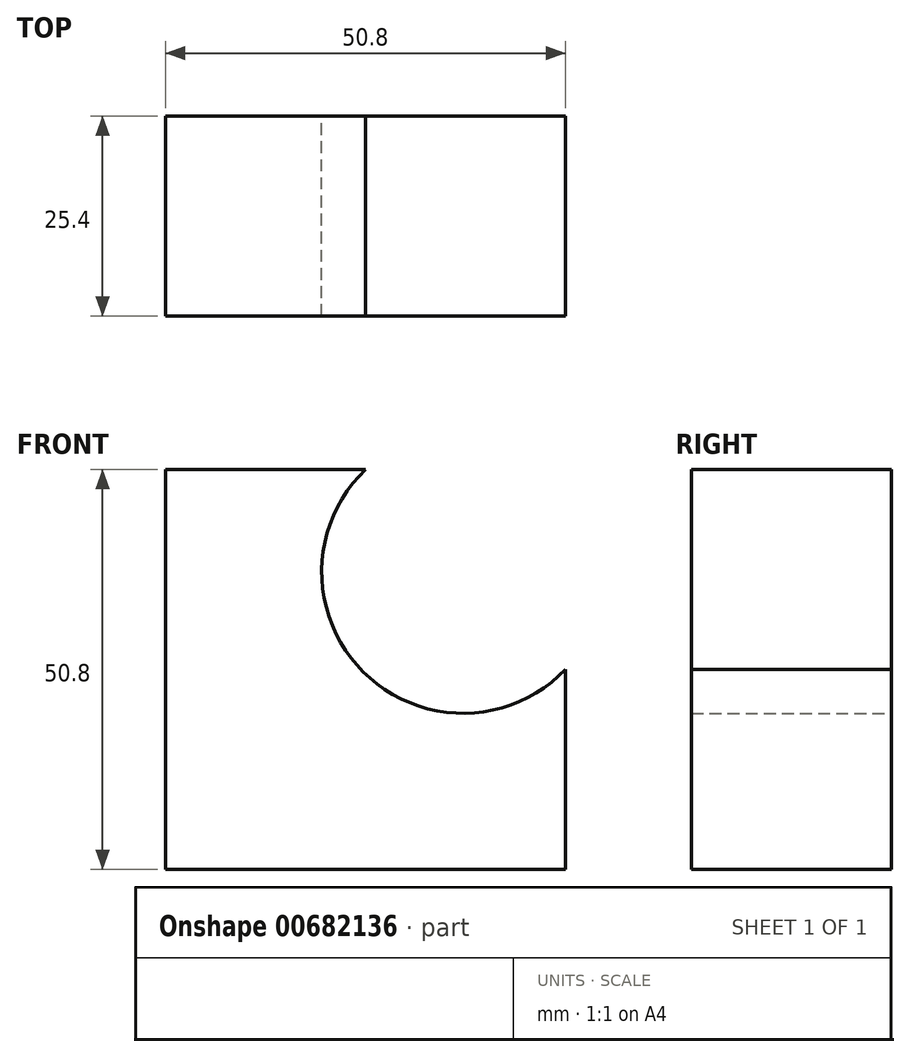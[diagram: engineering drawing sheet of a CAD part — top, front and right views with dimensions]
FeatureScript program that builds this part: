
annotation { "Feature Type Name" : "Feature", "Feature Type Description" : "" }
export const myFeature = defineFeature(function(context is Context, id is Id, definition is map)
    precondition{}
    {
        {
            var Q0;
            Q0=qCreatedBy(makeId("Front.planeOp"),FACE);
            var sketch = newSketch(context, id + "F0", { "sketchPlane" : qUnion([Q0])});
            skLineSegment(sketch, "E0", {"start": v(25.4, 30.77) * mm, "end": v(0, 30.77) * mm});
            skLineSegment(sketch, "E1", {"start": v(0, 30.77) * mm, "end": v(0, -20.03) * mm});
            skLineSegment(sketch, "E2", {"start": v(0, -20.03) * mm, "end": v(50.8, -20.03) * mm});
            skLineSegment(sketch, "E3", {"start": v(50.8, -20.03) * mm, "end": v(50.8, 5.37) * mm});
            skArc(sketch, "E4", {"start": v(25.4, 30.77) * mm, "mid": v(25.1, 5.07) * mm, "end": v(50.8, 5.37) * mm});
            skSolve(sketch);
        }
        {
            var Q0;
            Q0 = qSketchRegion(id + "F0", true);
            extrude(context, id + "F1", {"entities" : qUnion([Q0]), "depth" : 25.4 * mm, "offsetDistance" : 25.4 * mm});
        }
    });
